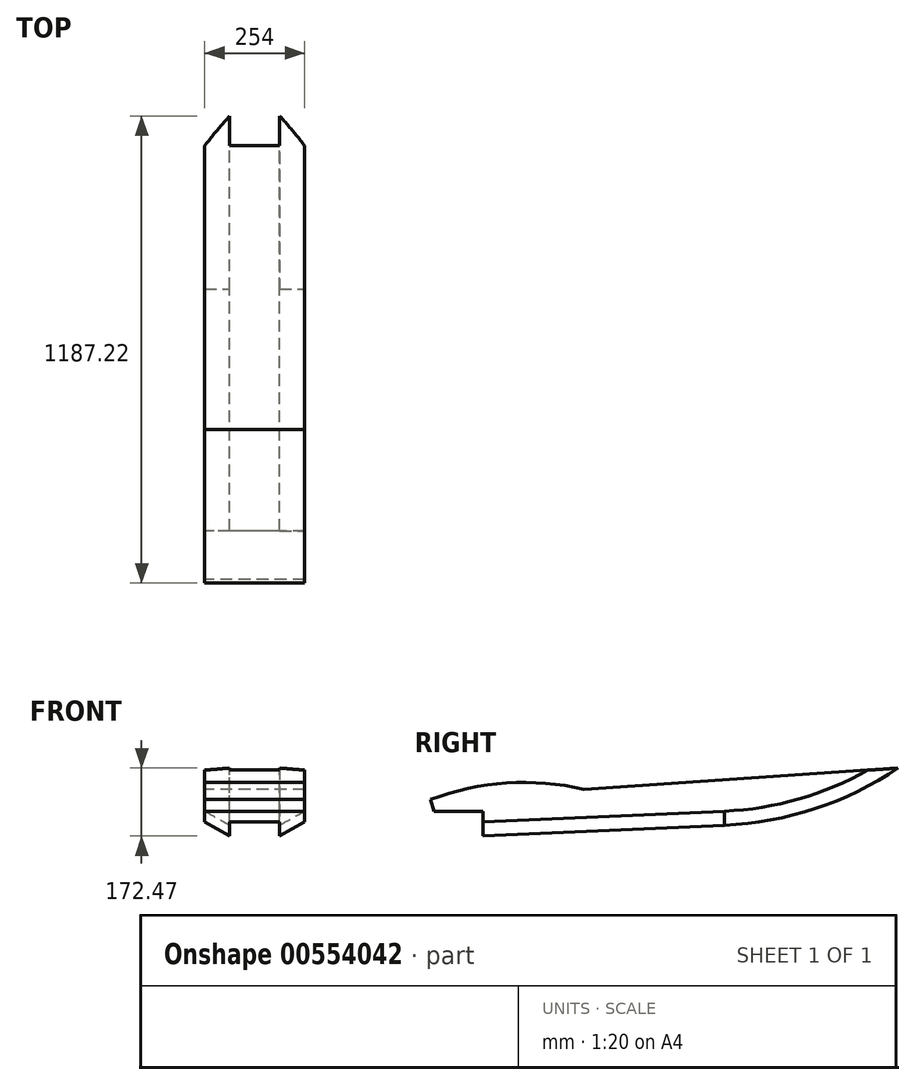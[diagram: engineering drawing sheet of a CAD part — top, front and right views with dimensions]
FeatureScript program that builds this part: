
annotation { "Feature Type Name" : "Feature", "Feature Type Description" : "" }
export const myFeature = defineFeature(function(context is Context, id is Id, definition is map)
    precondition{}
    {
        {
            var Q0;
            Q0=qCreatedBy(makeId("Right.planeOp"),FACE);
            var sketch = newSketch(context, id + "F0", { "sketchPlane" : qUnion([Q0])});
            skLineSegment(sketch, "E0", {"start": v(550.35, -81.18) * mm, "end": v(-238.98, -132.8) * mm});
            skArc(sketch, "E1", {"start": v(-238.98, -132.8) * mm, "mid": v(-435.8, -129.98) * mm, "end": v(-625.62, -182.14) * mm});
            skLineSegment(sketch, "E2", {"start": v(-625.62, -182.14) * mm, "end": v(-613, -223.44) * mm});
            skLineSegment(sketch, "E3", {"start": v(-613, -223.44) * mm, "end": v(-489.1, -223.44) * mm});
            skLineSegment(sketch, "E4", {"start": v(-489.1, -223.44) * mm, "end": v(-489.1, -250.98) * mm});
            skLineSegment(sketch, "E5", {"start": v(-489.1, -250.98) * mm, "end": v(124.7, -223.44) * mm});
            skArc(sketch, "E6", {"start": v(124.7, -223.44) * mm, "mid": v(347.47, -182.06) * mm, "end": v(550.35, -81.18) * mm});
            skSolve(sketch);
        }
        {
            var Q0;
            Q0 = qSketchRegion(id + "F0", true);
            extrude(context, id + "F1", {"entities" : qUnion([Q0]), "depth" : 254 * mm, "offsetDistance" : 25.4 * mm});
        }
        {
            var Q0;
            Q0=makeQuery(id+"F1.opExtrude","SWEPT_FACE",FACE,{"disambiguationData":[OSD([sQuery(id+"F0.wireOp",EDGE,"E4")])]});
            var sketch = newSketch(context, id + "F2", { "sketchPlane" : qUnion([Q0])});
            skLineSegment(sketch, "E7", {"start": v(0, -250.98) * mm, "end": v(127, -250.98) * mm, "construction": true});
            skLineSegment(sketch, "E8", {"start": v(127, -250.98) * mm, "end": v(254, -250.98) * mm, "construction": true});
            skLineSegment(sketch, "E9", {"start": v(254, -250.98) * mm, "end": v(190.5, -250.98) * mm, "construction": true});
            skLineSegment(sketch, "E10", {"start": v(190.5, -250.98) * mm, "end": v(127, -250.98) * mm, "construction": true});
            skLineSegment(sketch, "E11", {"start": v(127, -250.98) * mm, "end": v(63.5, -250.98) * mm, "construction": true});
            skLineSegment(sketch, "E12", {"start": v(63.5, -250.98) * mm, "end": v(63.5, -286.54) * mm});
            skLineSegment(sketch, "E13", {"start": v(63.5, -286.54) * mm, "end": v(0, -250.98) * mm});
            skLineSegment(sketch, "E14", {"start": v(127, -250.98) * mm, "end": v(127, -296.98) * mm, "construction": true});
            skLineSegment(sketch, "E15.MirrorCS", {"start": v(190.5, -250.98) * mm, "end": v(190.5, -286.54) * mm});
            skLineSegment(sketch, "E16.MirrorCS", {"start": v(190.5, -286.54) * mm, "end": v(254, -250.98) * mm});
            skSolve(sketch);
        }
        {
            var Q0;
            {var subQ0=sQuery(id+"F2.wireOp",EDGE,"E12");Q0=makeQuery(id+"F2.imprint","IMPRINT",FACE,{"disambiguationData":[TD([[makeQuery(id+"F2.imprint","IMPRINT",EDGE,{"derivedFrom":subQ0}),-1.0]])]});}
            var Q1;
            {var subQ0=sQuery(id+"F2.wireOp",EDGE,"E15.MirrorCS");Q1=makeQuery(id+"F2.imprint","IMPRINT",FACE,{"disambiguationData":[TD([[makeQuery(id+"F2.imprint","IMPRINT",EDGE,{"derivedFrom":subQ0}),1.0]])]});}
            var Q2;
            Q2=makeQuery(id+"F1.opExtrude","CAP_EDGE",EDGE,{"disambiguationData":[OSD([sQuery(id+"F0.wireOp",EDGE,"E5")])],"isStart":true});
            var Q3;
            Q3=makeQuery(id+"F1.opExtrude","CAP_EDGE",EDGE,{"disambiguationData":[OSD([sQuery(id+"F0.wireOp",EDGE,"E6")])],"isStart":true});
            sweep(context, id + "F3", {"operationType" : NewBodyOperationType.ADD, "profiles" : qUnion([Q0, Q1]), "path" : qUnion([Q2, Q3])});
        }
        {
            var Q0;
            Q0=makeQuery(id+"F1.opExtrude","CAP_FACE",FACE,{"disambiguationData":[OSD([sQuery(id+"F0.wireOp",EDGE,"E0"),sQuery(id+"F0.wireOp",EDGE,"E1"),sQuery(id+"F0.wireOp",EDGE,"E2"),sQuery(id+"F0.wireOp",EDGE,"E3"),sQuery(id+"F0.wireOp",EDGE,"E4"),sQuery(id+"F0.wireOp",EDGE,"E5"),sQuery(id+"F0.wireOp",EDGE,"E6")])],"isStart":true});
            var sketch = newSketch(context, id + "F4", { "sketchPlane" : qUnion([Q0])});
            skLineSegment(sketch, "E17", {"start": v(640.65, -195.02) * mm, "end": v(549.11, -11.93) * mm});
            skLineSegment(sketch, "E18", {"start": v(549.11, -11.93) * mm, "end": v(-511.24, 10.95) * mm});
            skLineSegment(sketch, "E19", {"start": v(-511.24, 10.95) * mm, "end": v(-584.14, -112.8) * mm});
            skArc(sketch, "E20", {"start": v(622.07, -193.77) * mm, "mid": v(429.01, -151.97) * mm, "end": v(232.1, -167.6) * mm});
            skLineSegment(sketch, "E21", {"start": v(-584.14, -112.8) * mm, "end": v(232.1, -167.6) * mm});
            skLineSegment(sketch, "E22", {"start": v(622.07, -193.77) * mm, "end": v(640.65, -195.02) * mm});
            skSolve(sketch);
        }
        {
            var Q0;
            Q0 = qSketchRegion(id + "F4", true);
            extrude(context, id + "F5", {"entities" : qUnion([Q0]), "operationType" : NewBodyOperationType.REMOVE, "oppositeDirection" : true, "depth" : 307.34 * mm, "offsetDistance" : 25.4 * mm});
        }
    });
